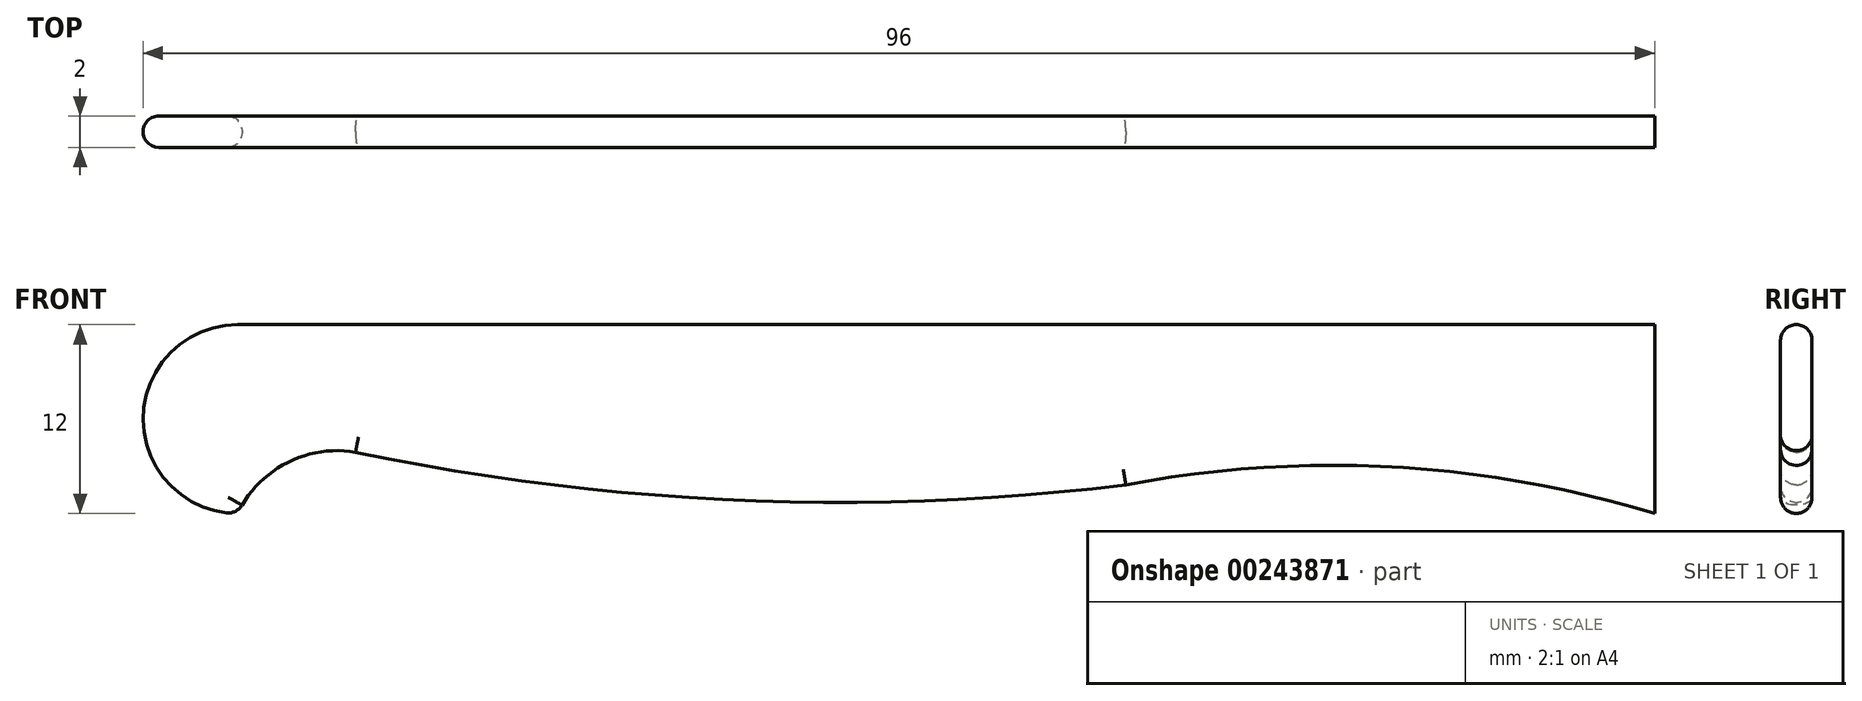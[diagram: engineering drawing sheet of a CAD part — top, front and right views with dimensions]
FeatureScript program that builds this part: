
annotation { "Feature Type Name" : "Feature", "Feature Type Description" : "" }
export const myFeature = defineFeature(function(context is Context, id is Id, definition is map)
    precondition{}
    {
        {
            var Q0;
            Q0=qCreatedBy(makeId("Front.planeOp"),FACE);
            var sketch = newSketch(context, id + "F0", { "sketchPlane" : qUnion([Q0])});
            skLineSegment(sketch, "E0.top", {"start": v(0, 12) * mm, "end": v(-90, 12) * mm});
            skLineSegment(sketch, "E0.left", {"start": v(0, 0) * mm, "end": v(0, 12) * mm});
            skArc(sketch, "E1", {"start": v(-90, 12) * mm, "mid": v(-96, 6) * mm, "end": v(-90, 0) * mm});
            skArc(sketch, "E2", {"start": v(0, 0) * mm, "mid": v(-16.68, 2.96) * mm, "end": v(-33.59, 1.82) * mm});
            skArc(sketch, "E3", {"start": v(-82.5, 3.9) * mm, "mid": v(-58.13, 0.85) * mm, "end": v(-33.59, 1.82) * mm});
            skArc(sketch, "E4", {"start": v(-82.5, 3.9) * mm, "mid": v(-86.9, 3.2) * mm, "end": v(-90, 0) * mm});
            skSolve(sketch);
        }
        {
            var Q0;
            Q0=makeQuery(id+"F0.imprint","IMPRINT",FACE,{"disambiguationData":[TD([[makeQuery(id+"F0.imprint","IMPRINT",EDGE,{"derivedFrom":sQuery(id+"F0.wireOp",EDGE,"E0.top")}),1.0]])]});
            extrude(context, id + "F1", {"entities" : qUnion([Q0]), "depth" : 2 * mm});
        }
        {
            var Q0;
            Q0=makeQuery(id+"F1.opExtrude","SWEPT_EDGE",EDGE,{"disambiguationData":[OSD([sQuery(id+"F0.wireOp",EDGE,"gm9K3XuQ-5Com-ai3Y-AobO-Ck4UlgHg72mD"),sQuery(id+"F0.wireOp",EDGE,"y1yC6GEc-8njZ-yeNI-HZw4-IEcQP5VU65Jo")])]});
            var Q1;
            Q1=makeQuery(id+"F1.opExtrude","CAP_EDGE",EDGE,{"disambiguationData":[OSD([sQuery(id+"F0.wireOp",EDGE,"E2")])],"isStart":false});
            var Q2;
            Q2=makeQuery(id+"F1.opExtrude","CAP_EDGE",EDGE,{"disambiguationData":[OSD([sQuery(id+"F0.wireOp",EDGE,"E3")])],"isStart":false});
            var Q3;
            Q3=makeQuery(id+"F1.opExtrude","CAP_EDGE",EDGE,{"disambiguationData":[OSD([sQuery(id+"F0.wireOp",EDGE,"E2")])],"isStart":true});
            var Q4;
            Q4=makeQuery(id+"F1.opExtrude","CAP_EDGE",EDGE,{"disambiguationData":[OSD([sQuery(id+"F0.wireOp",EDGE,"E3")])],"isStart":true});
            fillet(context, id + "F2", {"entities" : qUnion([Q0, Q1, Q2, Q3, Q4]), "radius" : 1 * mm, "tangentPropagation" : true, "allowEdgeOverflow" : false});
        }
        {
            var Q0;
            Q0=makeQuery(id+"F2.opFillet","BLEND_EDGE",EDGE,{"blendedFrom":[makeQuery(id+"F1.opExtrude","CAP_EDGE",EDGE,{"disambiguationData":[OSD([sQuery(id+"F0.wireOp",EDGE,"E4")])],"isStart":false}),makeQuery(id+"F1.opExtrude","SWEPT_FACE",FACE,{"disambiguationData":[OSD([sQuery(id+"F0.wireOp",EDGE,"E1")])]})],"blendedInto":[makeQuery(id+"F1.opExtrude","SWEPT_FACE",FACE,{"disambiguationData":[OSD([sQuery(id+"F0.wireOp",EDGE,"E1")])]})]});
            var Q1;
            Q1=makeQuery(id+"F2.opFillet","BLEND_EDGE",EDGE,{"blendedFrom":[makeQuery(id+"F1.opExtrude","CAP_EDGE",EDGE,{"disambiguationData":[OSD([sQuery(id+"F0.wireOp",EDGE,"E4")])],"isStart":true}),makeQuery(id+"F1.opExtrude","SWEPT_FACE",FACE,{"disambiguationData":[OSD([sQuery(id+"F0.wireOp",EDGE,"E1")])]})],"blendedInto":[makeQuery(id+"F1.opExtrude","SWEPT_FACE",FACE,{"disambiguationData":[OSD([sQuery(id+"F0.wireOp",EDGE,"E1")])]})]});
            fillet(context, id + "F3", {"entities" : qUnion([Q0, Q1]), "radius" : 1 * mm, "tangentPropagation" : true, "allowEdgeOverflow" : false});
        }
    });
